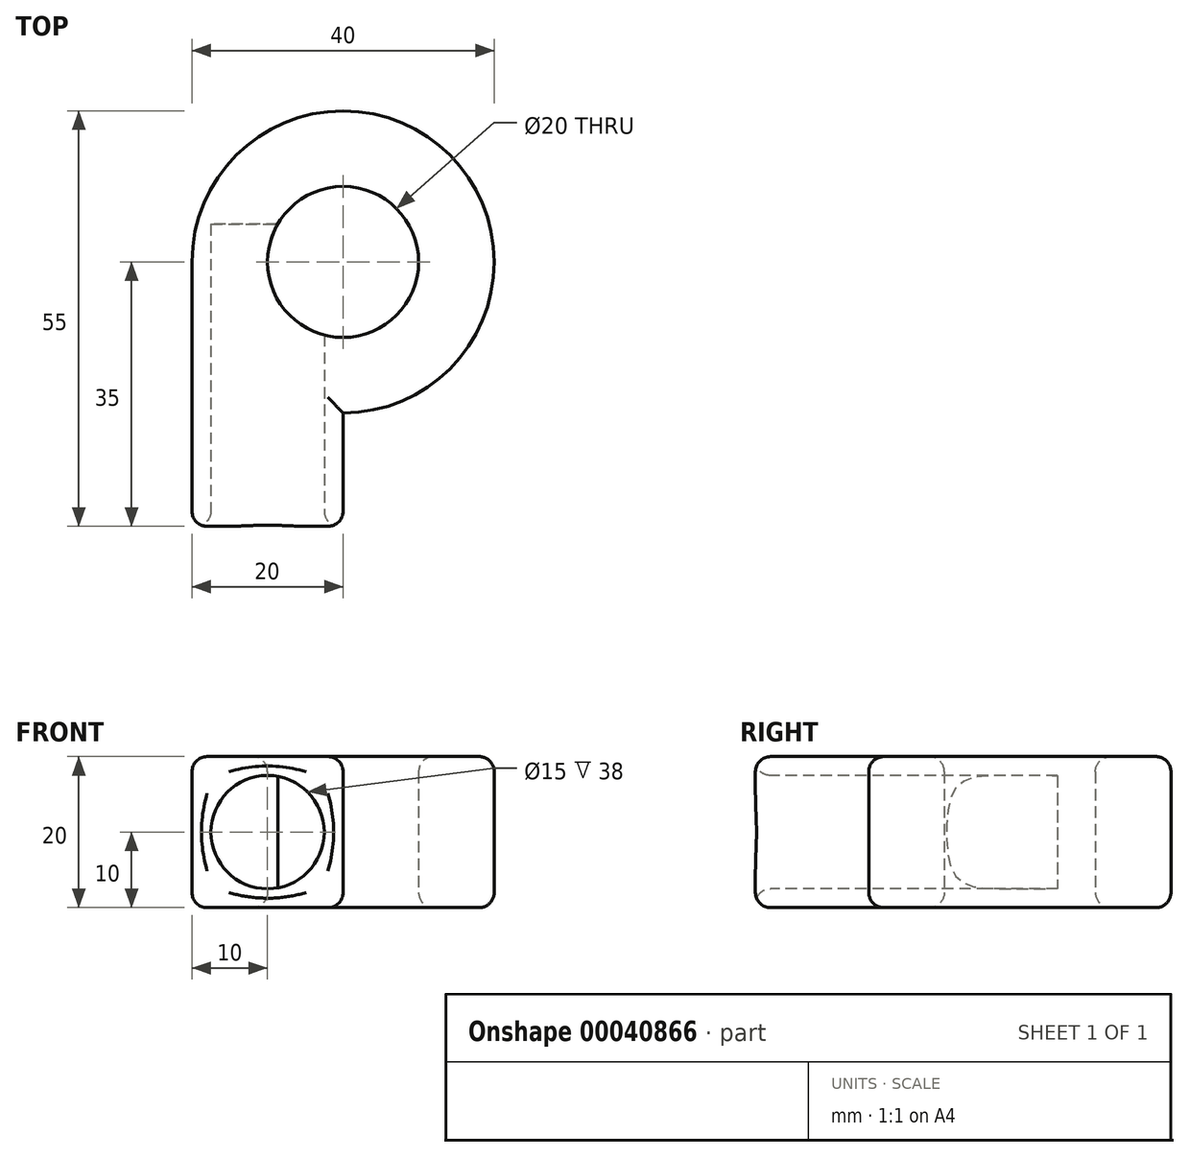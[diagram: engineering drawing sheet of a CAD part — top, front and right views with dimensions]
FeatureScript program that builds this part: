
annotation { "Feature Type Name" : "Feature", "Feature Type Description" : "" }
export const myFeature = defineFeature(function(context is Context, id is Id, definition is map)
    precondition{}
    {
        {
            var Q0;
            Q0=qCreatedBy(makeId("Top.planeOp"),FACE);
            var sketch = newSketch(context, id + "F0", { "sketchPlane" : qUnion([Q0])});
            skArc(sketch, "E0", {"start": v(0, -20) * mm, "mid": v(14.14, 14.14) * mm, "end": v(-20, 0) * mm});
            skCircle(sketch, "E1", {"center": v(0, 0) * mm, "radius": 10 * mm});
            skLineSegment(sketch, "E2", {"start": v(0, -20) * mm, "end": v(0, -35) * mm});
            skLineSegment(sketch, "E3", {"start": v(0, -35) * mm, "end": v(-20, -35) * mm});
            skLineSegment(sketch, "E4", {"start": v(-20, -35) * mm, "end": v(-20, 0) * mm});
            skSolve(sketch);
        }
        {
            var Q0;
            Q0=makeQuery(id+"F0.imprint","IMPRINT",FACE,{"disambiguationData":[TD([[makeQuery(id+"F0.imprint","IMPRINT",EDGE,{"derivedFrom":sQuery(id+"F0.wireOp",EDGE,"E0")}),1.0]])]});
            extrude(context, id + "F1", {"entities" : qUnion([Q0]), "depth" : 20 * mm});
        }
        {
            var Q0;
            Q0=makeQuery(id+"F1.opExtrude","SWEPT_FACE",FACE,{"disambiguationData":[OSD([sQuery(id+"F0.wireOp",EDGE,"E3")])]});
            var sketch = newSketch(context, id + "F2", { "sketchPlane" : qUnion([Q0])});
            skCircle(sketch, "E5", {"center": v(-10, 10) * mm, "radius": 7.5 * mm});
            skLineSegment(sketch, "E6", {"start": v(-20, 20) * mm, "end": v(0, 0) * mm, "construction": true});
            skLineSegment(sketch, "E7", {"start": v(0, 20) * mm, "end": v(-20, 0) * mm, "construction": true});
            skSolve(sketch);
        }
        {
            var Q0;
            Q0 = qSketchRegion(id + "F2", true);
            extrude(context, id + "F3", {"entities" : qUnion([Q0]), "operationType" : NewBodyOperationType.REMOVE, "oppositeDirection" : true, "depth" : 40 * mm});
        }
        {
            var Q0;
            Q0=makeQuery(id+"F1.opExtrude","CAP_FACE",FACE,{"disambiguationData":[OSD([sQuery(id+"F0.wireOp",EDGE,"E0"),sQuery(id+"F0.wireOp",EDGE,"E1"),sQuery(id+"F0.wireOp",EDGE,"E2"),sQuery(id+"F0.wireOp",EDGE,"E3"),sQuery(id+"F0.wireOp",EDGE,"E4")])],"isStart":false});
            var Q1;
            Q1=makeQuery(id+"F1.opExtrude","SWEPT_FACE",FACE,{"disambiguationData":[OSD([sQuery(id+"F0.wireOp",EDGE,"E3")])]});
            var Q2;
            Q2=makeQuery(id+"F1.opExtrude","CAP_FACE",FACE,{"disambiguationData":[OSD([sQuery(id+"F0.wireOp",EDGE,"E0"),sQuery(id+"F0.wireOp",EDGE,"E1"),sQuery(id+"F0.wireOp",EDGE,"E2"),sQuery(id+"F0.wireOp",EDGE,"E3"),sQuery(id+"F0.wireOp",EDGE,"E4")])],"isStart":true});
            fillet(context, id + "F4", {"entities" : qUnion([Q0, Q1, Q2]), "radius" : 2 * mm, "tangentPropagation" : true, "allowEdgeOverflow" : false});
        }
    });
